# Revit family: IS_Iom_A9133_BIM_IT
name_source: partatom
category: Plumbing Fixtures
revit_build: Autodesk Revit 2017 (Build: 20160225_1515(x64)
units: mm (PartAtom-declared; Revit-internal decimal feet)

## family parameters
Always vertical = No
Cut with Voids When Loaded = No
OmniClass Number = 23.45.05.14.21.11
OmniClass Title = Bath/Shower Units
Part Type = Normal
Room Calculation Point = No
Round Connector Dimension = Use Diameter
Shared = No
Work Plane-Based = No

## types (1)
- A9133MY - IOM HLDR POL S/S FOR TISSUE
    Accessori = www.idealstandard.it
    AltezzaNominale = 157 mm
    Autore = Ideal Standard
    BIMobject category = Toilets
    BIMobject category code = sanitary-toilets
    BIMobject main category = Sanitary
    BIMobject main category code = sanitary
    BOSUseNativeGeometries = 1
    Brand = Ideal Standard
    Brand url = http://www.idealstandard.it
    Caratteristiche = IOM HLDR POL S/S FOR TISSUE
    CodiceABarre = 4015413328142
    CodiceDiPrestazione = EN
    Colore = Acciaio Lucido
    Connessione = piombatura
    CostoDiSostituzione = 0 $
    Date of publishing = 2019_01_04
    Description = IOM HLDR POL S/S FOR TISSUE
    Desrizione = IOM HLDR POL S/S FOR TISSUE
    DimensioneScarico = 0
    EAN code = https://4015413328142
    Edition number = 1
    Finitura = Acciaio Lucido
    Forma = scolpito
    Garanzia = Garanzia Ideal Standard
    Grado = n/s
    IFC Classification = IfcSanitaryTerminal
    IfcEsportaCome = SanitaryTerminal
    InformazioniDiProdotto = http://www.idealstandard.it
    Installation instructions = http://www.idealstandard.it
    Installazione = http://www.idealstandard.it
    InstruzioniInstallazione = http://www.idealstandard.it
    LarghezzaNominale = 0 mm  [stored 0 ft]
    LunghezzaNominale = 58 mm
    Maniglia = No
    Manufacturer name = Ideal Standard
    Material main = brass
    Materiale = Ottone
    Model = A9133MY
    NBS Reference Code = Pr_40_20_87_75
    NBS Reference Description = Shower fitting package
    Nominal depth = 0
    Nominal height = 0
    NominalHeight = 157 mm
    NominalLength = 58 mm
    NominalWidth = 297 mm
    NumeroDiModello = A9110MY
    OmniClass Code = 23-31 19 00
    OmniClass Description = Toilets
    PartiDiRicambio = http://www.idealstandard.it
    PiattoDoccia = No
    Product Guid = 9cb783d7-6250-4dc7-81a8-9ea60c20cec8
    Product SKU = A9133
    Product certification = http://www.idealstandard.it
    Product data url = https://bimobject.com
    Product family = Sanitary
    Product group = Toilet Roll Holders
    Product name = IOM HLDR POL S/S FOR TISSUE
    Product url = http://www.idealstandard.it
    ProfonditaNominale = 0 mm  [stored 0 ft]
    QR code = http://bimobject.com
    Revisione = 1
    SeatMaterial = 0 mm  [stored 0 ft]
    Size = 157 x 58 x 297mm
    SpessoreDelMateriale = 0
    SpilloverLivello = 0
    Technical description = http://www.idealstandard.it
    Telefono = 800 652 290
    TipoDiDato = Fisso
    TipoEspotazioneIfc = IfcSanitaryTerminalType
    URL = http://www.idealstandard.it
    Uniclass 1.4 Code = L7216
    Uniclass 1.4 Description = Toilets
    Uniclass 2.0 Code = SS-35-65-90
    Uniclass 2.0 Description = Toilet Systems
    UnitàDurata = anni
    UnitàDurataGaranzia = anni
    UnitàLineare = millimetri
    UnitàMonetaria = €
    UnitàSuperficie = €
    UnitàVolume = millimetri
    Versione = 1
    VersioneClassificazioneUni2015 = 1
    Weight Net (Kg) = 0
    Youtube clip = https://www.youtube.com

note: [stored X ft] marks values corroborated as IEEE doubles in the binary element streams (Revit-internal decimal feet)

## geometry (parser evidence)
native form markers: Sweep x1
no freeform markers — native parametric forms only
